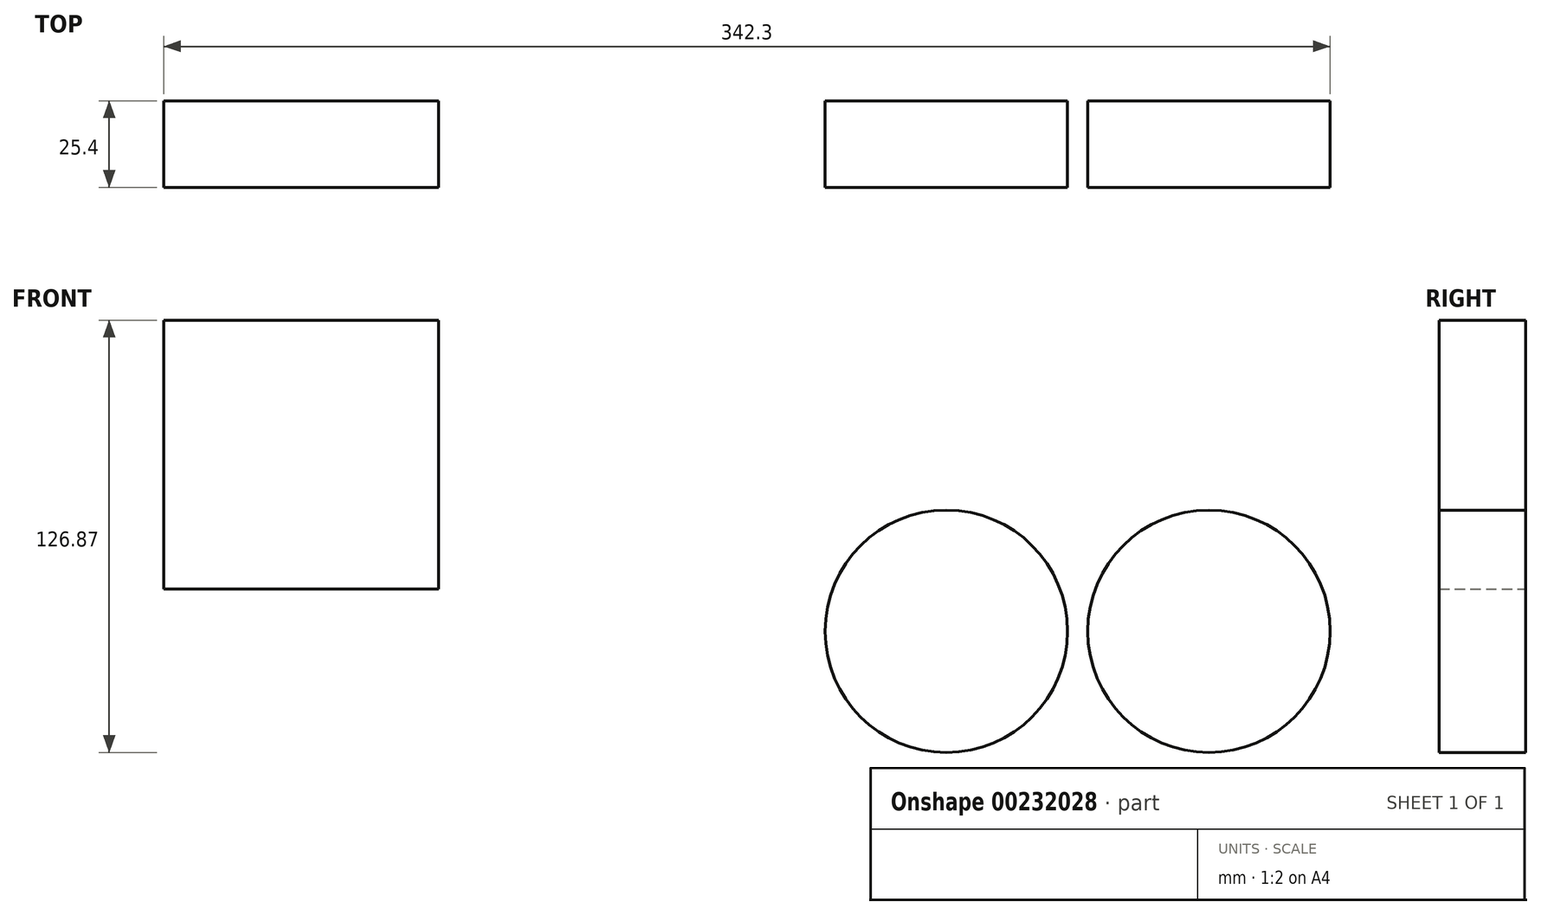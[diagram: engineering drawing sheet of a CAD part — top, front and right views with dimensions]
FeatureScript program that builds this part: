
annotation { "Feature Type Name" : "Feature", "Feature Type Description" : "" }
export const myFeature = defineFeature(function(context is Context, id is Id, definition is map)
    precondition{}
    {
        {
            var Q0;
            Q0=qCreatedBy(makeId("Front.planeOp"),FACE);
            var sketch = newSketch(context, id + "F0", { "sketchPlane" : qUnion([Q0])});
            skCircle(sketch, "E0", {"center": v(0, -44.48) * mm, "radius": 35.56 * mm});
            skPoint(sketch, "E1.center", {"position": v(0, 0) * mm});
            skCircle(sketch, "E2.1.0", {"center": v(38.52, 22.24) * mm, "radius": 35.56 * mm});
            skCircle(sketch, "E2.2.0", {"center": v(-38.52, 22.24) * mm, "radius": 35.56 * mm});
            skSolve(sketch);
        }
        {
            var Q0;
            Q0=makeQuery(id+"F0.imprint","IMPRINT",FACE,{"disambiguationData":[TD([[makeQuery(id+"F0.imprint","IMPRINT",EDGE,{"derivedFrom":sQuery(id+"F0.wireOp",EDGE,"E2.2.0")}),1.0]])]});
            var Q1;
            Q1=makeQuery(id+"F0.imprint","IMPRINT",FACE,{"disambiguationData":[TD([[makeQuery(id+"F0.imprint","IMPRINT",EDGE,{"derivedFrom":sQuery(id+"F0.wireOp",EDGE,"E2.1.0")}),1.0]])]});
            var Q2;
            Q2=makeQuery(id+"F0.imprint","IMPRINT",FACE,{"disambiguationData":[TD([[makeQuery(id+"F0.imprint","IMPRINT",EDGE,{"derivedFrom":sQuery(id+"F0.wireOp",EDGE,"E0")}),1.0]])]});
            extrude(context, id + "F1", {"entities" : qUnion([Q0, Q1, Q2]), "depth" : 25.4 * mm});
        }
        {
            var Q0;
            Q0=makeQuery(id+"F1.opExtrude","SWEPT_BODY",BODY,{"disambiguationData":[OSD([sQuery(id+"F0.wireOp",EDGE,"E0")])]});
            deleteBodies(context, id + "F2", {"entities" : qUnion([Q0])});
        }
        {
            var Q0;
            Q0=qCreatedBy(makeId("Front.planeOp"),FACE);
            var sketch = newSketch(context, id + "F3", { "sketchPlane" : qUnion([Q0])});
            skLineSegment(sketch, "E3.bottom", {"start": v(-268.21, 113.55) * mm, "end": v(-187.54, 113.55) * mm});
            skLineSegment(sketch, "E3.top", {"start": v(-268.21, 34.6) * mm, "end": v(-187.54, 34.6) * mm});
            skLineSegment(sketch, "E3.left", {"start": v(-268.21, 113.55) * mm, "end": v(-268.21, 34.6) * mm});
            skLineSegment(sketch, "E3.right", {"start": v(-187.54, 113.55) * mm, "end": v(-187.54, 34.6) * mm});
            skSolve(sketch);
        }
        {
            var Q0;
            Q0=makeQuery(id+"F3.imprint","IMPRINT",FACE,{"disambiguationData":[TD([[makeQuery(id+"F3.imprint","IMPRINT",EDGE,{"derivedFrom":sQuery(id+"F3.wireOp",EDGE,"E3.bottom")}),-1.0]])]});
            extrude(context, id + "F4", {"entities" : qUnion([Q0]), "depth" : 25.4 * mm});
        }
    });
